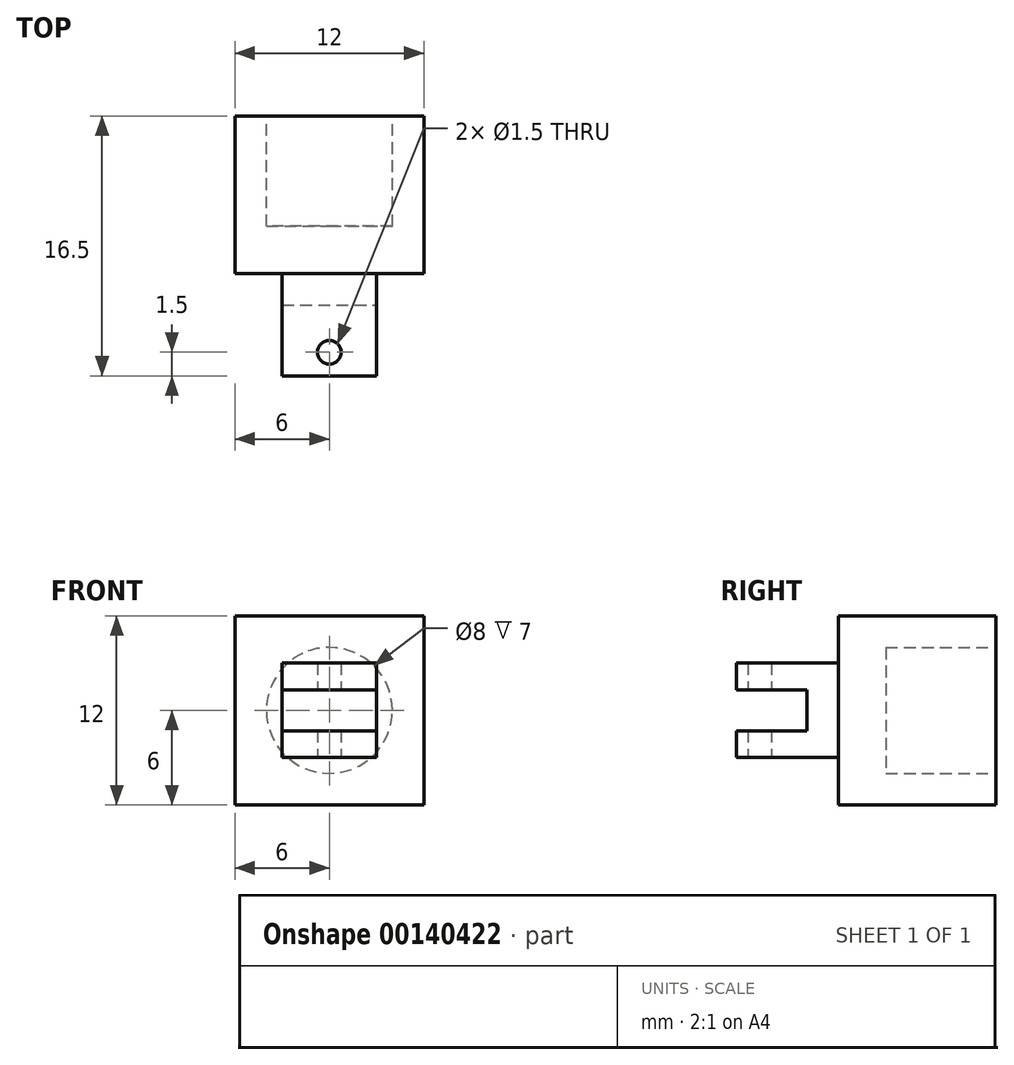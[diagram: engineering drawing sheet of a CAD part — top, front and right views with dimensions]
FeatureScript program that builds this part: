
annotation { "Feature Type Name" : "Feature", "Feature Type Description" : "" }
export const myFeature = defineFeature(function(context is Context, id is Id, definition is map)
    precondition{}
    {
        {
            var Q0;
            Q0=qCreatedBy(makeId("Top.planeOp"),FACE);
            var sketch = newSketch(context, id + "F0", { "sketchPlane" : qUnion([Q0])});
            skCircle(sketch, "E0", {"center": v(0, 0) * mm, "radius": 0.75 * mm});
            skLineSegment(sketch, "E1.bottom", {"start": v(-3, 5) * mm, "end": v(3, 5) * mm});
            skLineSegment(sketch, "E1.top", {"start": v(-3, -1.5) * mm, "end": v(3, -1.5) * mm});
            skLineSegment(sketch, "E1.left", {"start": v(-3, 5) * mm, "end": v(-3, -1.5) * mm});
            skLineSegment(sketch, "E1.right", {"start": v(3, 5) * mm, "end": v(3, -1.5) * mm});
            skSolve(sketch);
        }
        {
            var Q0;
            Q0 = qSketchRegion(id + "F0", true);
            extrude(context, id + "F1", {"entities" : qUnion([Q0]), "endBound" : BoundingType.SYMMETRIC, "depth" : 6 * mm});
        }
        {
            var Q0;
            Q0=qCreatedBy(makeId("Top.planeOp"),FACE);
            var sketch = newSketch(context, id + "F2", { "sketchPlane" : qUnion([Q0])});
            skLineSegment(sketch, "E2.bottom", {"start": v(-3, 3) * mm, "end": v(3, 3) * mm});
            skLineSegment(sketch, "E2.top", {"start": v(-3, -3) * mm, "end": v(3, -3) * mm});
            skLineSegment(sketch, "E2.left", {"start": v(-3, 3) * mm, "end": v(-3, -3) * mm});
            skLineSegment(sketch, "E2.right", {"start": v(3, 3) * mm, "end": v(3, -3) * mm});
            skSolve(sketch);
        }
        {
            var Q0;
            Q0 = qSketchRegion(id + "F2", true);
            extrude(context, id + "F3", {"entities" : qUnion([Q0]), "operationType" : NewBodyOperationType.REMOVE, "endBound" : BoundingType.SYMMETRIC, "oppositeDirection" : true, "depth" : 2.6 * mm});
        }
        {
            var Q0;
            Q0=makeQuery(id+"F1.opExtrude","SWEPT_FACE",FACE,{"disambiguationData":[OSD([sQuery(id+"F0.wireOp",EDGE,"E1.bottom")])]});
            var sketch = newSketch(context, id + "F4", { "sketchPlane" : qUnion([Q0])});
            skLineSegment(sketch, "E3.bottom", {"start": v(-6, -6) * mm, "end": v(6, -6) * mm});
            skLineSegment(sketch, "E3.top", {"start": v(-6, 6) * mm, "end": v(6, 6) * mm});
            skLineSegment(sketch, "E3.left", {"start": v(-6, -6) * mm, "end": v(-6, 6) * mm});
            skLineSegment(sketch, "E3.right", {"start": v(6, -6) * mm, "end": v(6, 6) * mm});
            skPoint(sketch, "E3.middle", {"position": v(0, 0) * mm});
            skSolve(sketch);
        }
        {
            var Q0;
            Q0 = qSketchRegion(id + "F4", true);
            extrude(context, id + "F5", {"entities" : qUnion([Q0]), "operationType" : NewBodyOperationType.ADD, "depth" : 10 * mm});
        }
        {
            var Q0;
            Q0=makeQuery(id+"F5.opExtrude","CAP_FACE",FACE,{"disambiguationData":[OSD([sQuery(id+"F4.wireOp",EDGE,"E3.bottom"),sQuery(id+"F4.wireOp",EDGE,"E3.top"),sQuery(id+"F4.wireOp",EDGE,"E3.left"),sQuery(id+"F4.wireOp",EDGE,"E3.right")])],"isStart":false});
            var sketch = newSketch(context, id + "F6", { "sketchPlane" : qUnion([Q0])});
            skCircle(sketch, "E4", {"center": v(0, 0) * mm, "radius": 4 * mm});
            skSolve(sketch);
        }
        {
            var Q0;
            Q0 = qSketchRegion(id + "F6", true);
            extrude(context, id + "F7", {"entities" : qUnion([Q0]), "operationType" : NewBodyOperationType.REMOVE, "oppositeDirection" : true, "depth" : 7 * mm});
        }
    });
